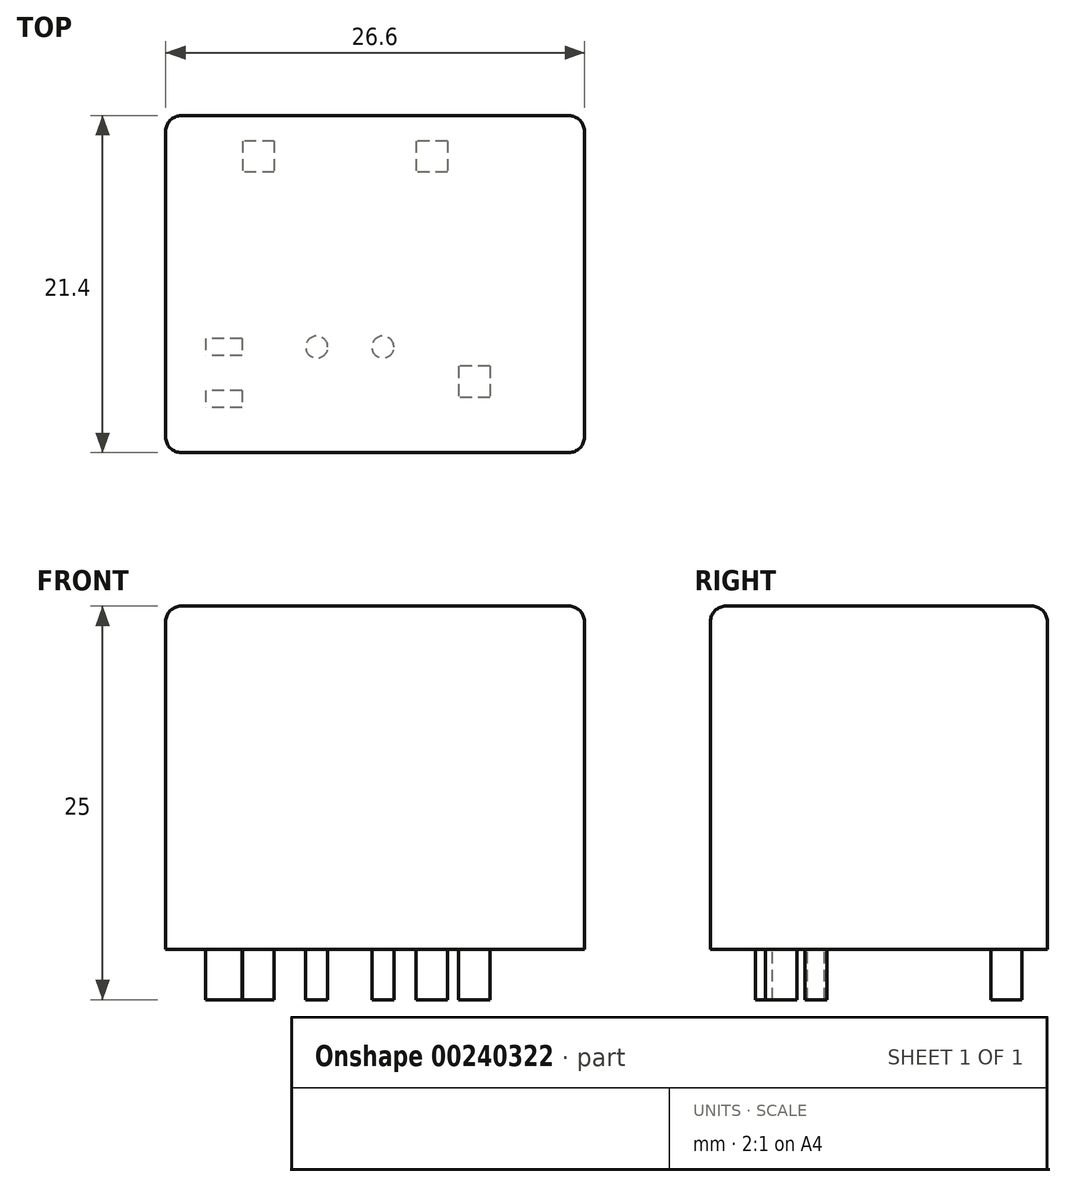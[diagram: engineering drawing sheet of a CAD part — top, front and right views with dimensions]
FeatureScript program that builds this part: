
annotation { "Feature Type Name" : "Feature", "Feature Type Description" : "" }
export const myFeature = defineFeature(function(context is Context, id is Id, definition is map)
    precondition{}
    {
        {
            var Q0;
            Q0=qCreatedBy(makeId("Top.planeOp"),FACE);
            var sketch = newSketch(context, id + "F0", { "sketchPlane" : qUnion([Q0])});
            skCircle(sketch, "E0", {"center": v(0, 0) * mm, "radius": 0.7 * mm});
            skCircle(sketch, "E1", {"center": v(4.2, 0) * mm, "radius": 0.7 * mm});
            skLineSegment(sketch, "E2.bottom", {"start": v(-4.75, 0.55) * mm, "end": v(-7.05, 0.55) * mm});
            skLineSegment(sketch, "E2.top", {"start": v(-4.75, -0.55) * mm, "end": v(-7.05, -0.55) * mm});
            skLineSegment(sketch, "E2.left", {"start": v(-4.75, 0.55) * mm, "end": v(-4.75, -0.55) * mm});
            skLineSegment(sketch, "E2.right", {"start": v(-7.05, 0.55) * mm, "end": v(-7.05, -0.55) * mm});
            skPoint(sketch, "E2.middle", {"position": v(-5.9, 0) * mm});
            skLineSegment(sketch, "E3.bottom", {"start": v(-4.75, -2.75) * mm, "end": v(-7.05, -2.75) * mm});
            skLineSegment(sketch, "E3.top", {"start": v(-4.75, -3.85) * mm, "end": v(-7.05, -3.85) * mm});
            skLineSegment(sketch, "E3.left", {"start": v(-4.75, -2.75) * mm, "end": v(-4.75, -3.85) * mm});
            skLineSegment(sketch, "E3.right", {"start": v(-7.05, -2.75) * mm, "end": v(-7.05, -3.85) * mm});
            skPoint(sketch, "E3.middle", {"position": v(-5.9, -3.3) * mm});
            skLineSegment(sketch, "E4.bottom", {"start": v(11, -1.2) * mm, "end": v(9, -1.2) * mm});
            skLineSegment(sketch, "E4.top", {"start": v(11, -3.2) * mm, "end": v(9, -3.2) * mm});
            skLineSegment(sketch, "E4.left", {"start": v(11, -1.2) * mm, "end": v(11, -3.2) * mm});
            skLineSegment(sketch, "E4.right", {"start": v(9, -1.2) * mm, "end": v(9, -3.2) * mm});
            skPoint(sketch, "E4.middle", {"position": v(10, -2.2) * mm});
            skLineSegment(sketch, "E5.bottom", {"start": v(8.3, 13.1) * mm, "end": v(6.3, 13.1) * mm});
            skLineSegment(sketch, "E5.top", {"start": v(8.3, 11.1) * mm, "end": v(6.3, 11.1) * mm});
            skLineSegment(sketch, "E5.left", {"start": v(8.3, 13.1) * mm, "end": v(8.3, 11.1) * mm});
            skLineSegment(sketch, "E5.right", {"start": v(6.3, 13.1) * mm, "end": v(6.3, 11.1) * mm});
            skPoint(sketch, "E5.middle", {"position": v(7.3, 12.1) * mm});
            skLineSegment(sketch, "E6.bottom", {"start": v(-2.7, 13.1) * mm, "end": v(-4.7, 13.1) * mm});
            skLineSegment(sketch, "E6.top", {"start": v(-2.7, 11.1) * mm, "end": v(-4.7, 11.1) * mm});
            skLineSegment(sketch, "E6.left", {"start": v(-2.7, 13.1) * mm, "end": v(-2.7, 11.1) * mm});
            skLineSegment(sketch, "E6.right", {"start": v(-4.7, 13.1) * mm, "end": v(-4.7, 11.1) * mm});
            skPoint(sketch, "E6.middle", {"position": v(-3.7, 12.1) * mm});
            skSolve(sketch);
        }
        {
            var Q0;
            Q0=qCreatedBy(makeId("Top.planeOp"),FACE);
            var sketch = newSketch(context, id + "F1", { "sketchPlane" : qUnion([Q0])});
            skLineSegment(sketch, "E7.bottom", {"start": v(-8.6, -6.7) * mm, "end": v(16, -6.7) * mm});
            skLineSegment(sketch, "E7.top", {"start": v(-8.6, 14.7) * mm, "end": v(16, 14.7) * mm});
            skLineSegment(sketch, "E7.left", {"start": v(-9.6, -5.7) * mm, "end": v(-9.6, 13.7) * mm});
            skLineSegment(sketch, "E7.right", {"start": v(17, -5.7) * mm, "end": v(17, 13.7) * mm});
            skPoint(sketch, "E8.visualSharp", {"position": v(17, -6.7) * mm});
            skArc(sketch, "E8.filletArc", {"start": v(16, -6.7) * mm, "mid": v(16.7, -6.4) * mm, "end": v(17, -5.7) * mm});
            skPoint(sketch, "E9.visualSharp", {"position": v(17, 14.7) * mm});
            skArc(sketch, "E9.filletArc", {"start": v(17, 13.7) * mm, "mid": v(16.7, 14.4) * mm, "end": v(16, 14.7) * mm});
            skPoint(sketch, "E10.visualSharp", {"position": v(-9.6, 14.7) * mm});
            skArc(sketch, "E10.filletArc", {"start": v(-8.6, 14.7) * mm, "mid": v(-9.3, 14.4) * mm, "end": v(-9.6, 13.7) * mm});
            skPoint(sketch, "E11.visualSharp", {"position": v(-9.6, -6.7) * mm});
            skArc(sketch, "E11.filletArc", {"start": v(-9.6, -5.7) * mm, "mid": v(-9.3, -6.4) * mm, "end": v(-8.6, -6.7) * mm});
            skSolve(sketch);
        }
        {
            var Q0;
            Q0=makeQuery(id+"F1.imprint","IMPRINT",FACE,{"disambiguationData":[TD([[makeQuery(id+"F1.imprint","IMPRINT",EDGE,{"derivedFrom":sQuery(id+"F1.wireOp",EDGE,"E7.bottom")}),1.0]])]});
            extrude(context, id + "F2", {"entities" : qUnion([Q0]), "depth" : 21.8 * mm});
        }
        {
            var Q0;
            Q0=makeQuery(id+"F0.imprint","IMPRINT",FACE,{"disambiguationData":[TD([[makeQuery(id+"F0.imprint","IMPRINT",EDGE,{"derivedFrom":sQuery(id+"F0.wireOp",EDGE,"E4.bottom")}),1.0]])]});
            var Q1;
            Q1=makeQuery(id+"F0.imprint","IMPRINT",FACE,{"disambiguationData":[TD([[makeQuery(id+"F0.imprint","IMPRINT",EDGE,{"derivedFrom":sQuery(id+"F0.wireOp",EDGE,"E5.bottom")}),1.0]])]});
            var Q2;
            Q2=makeQuery(id+"F0.imprint","IMPRINT",FACE,{"disambiguationData":[TD([[makeQuery(id+"F0.imprint","IMPRINT",EDGE,{"derivedFrom":sQuery(id+"F0.wireOp",EDGE,"E1")}),1.0]])]});
            var Q3;
            Q3=makeQuery(id+"F0.imprint","IMPRINT",FACE,{"disambiguationData":[TD([[makeQuery(id+"F0.imprint","IMPRINT",EDGE,{"derivedFrom":sQuery(id+"F0.wireOp",EDGE,"E0")}),1.0]])]});
            var Q4;
            Q4=makeQuery(id+"F0.imprint","IMPRINT",FACE,{"disambiguationData":[TD([[makeQuery(id+"F0.imprint","IMPRINT",EDGE,{"derivedFrom":sQuery(id+"F0.wireOp",EDGE,"E3.bottom")}),1.0]])]});
            var Q5;
            Q5=makeQuery(id+"F0.imprint","IMPRINT",FACE,{"disambiguationData":[TD([[makeQuery(id+"F0.imprint","IMPRINT",EDGE,{"derivedFrom":sQuery(id+"F0.wireOp",EDGE,"E2.bottom")}),1.0]])]});
            var Q6;
            Q6=makeQuery(id+"F0.imprint","IMPRINT",FACE,{"disambiguationData":[TD([[makeQuery(id+"F0.imprint","IMPRINT",EDGE,{"derivedFrom":sQuery(id+"F0.wireOp",EDGE,"E6.bottom")}),1.0]])]});
            extrude(context, id + "F3", {"entities" : qUnion([Q0, Q1, Q2, Q3, Q4, Q5, Q6]), "oppositeDirection" : true, "depth" : 3.2 * mm});
        }
        {
            var Q0;
            Q0=makeQuery(id+"F2.opExtrude","CAP_FACE",FACE,{"disambiguationData":[OSD([sQuery(id+"F1.wireOp",EDGE,"E7.bottom"),sQuery(id+"F1.wireOp",EDGE,"E7.top"),sQuery(id+"F1.wireOp",EDGE,"E7.left"),sQuery(id+"F1.wireOp",EDGE,"E7.right"),sQuery(id+"F1.wireOp",EDGE,"E8.filletArc"),sQuery(id+"F1.wireOp",EDGE,"E9.filletArc"),sQuery(id+"F1.wireOp",EDGE,"E10.filletArc"),sQuery(id+"F1.wireOp",EDGE,"E11.filletArc")])],"isStart":false});
            fillet(context, id + "F4", {"entities" : qUnion([Q0]), "radius" : 1 * mm, "tangentPropagation" : true, "allowEdgeOverflow" : false});
        }
    });
